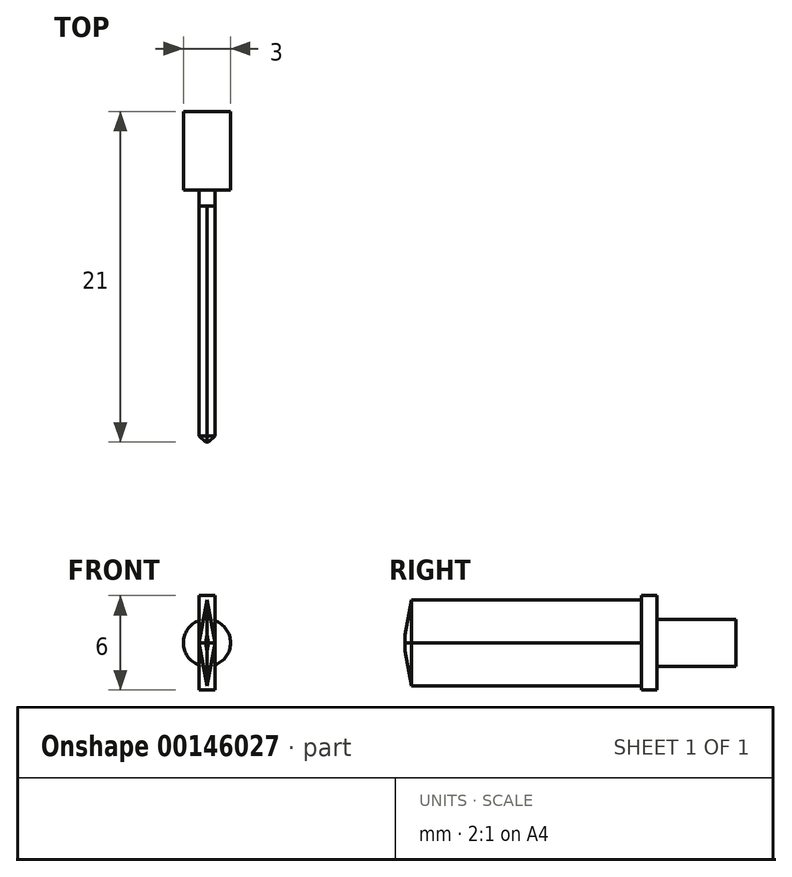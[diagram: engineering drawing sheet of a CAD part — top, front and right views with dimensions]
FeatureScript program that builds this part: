
annotation { "Feature Type Name" : "Feature", "Feature Type Description" : "" }
export const myFeature = defineFeature(function(context is Context, id is Id, definition is map)
    precondition{}
    {
        {
            var Q0;
            Q0=qCreatedBy(makeId("Front.planeOp"),FACE);
            var sketch = newSketch(context, id + "F0", { "sketchPlane" : qUnion([Q0])});
            skCircle(sketch, "E0", {"center": v(0, 0) * mm, "radius": 1.5 * mm});
            skSolve(sketch);
        }
        {
            var Q0;
            Q0 = qSketchRegion(id + "F0", true);
            extrude(context, id + "F1", {"entities" : qUnion([Q0]), "depth" : 5 * mm});
        }
        {
            var Q0;
            Q0=makeQuery(id+"F1.opExtrude","CAP_FACE",FACE,{"disambiguationData":[OSD([sQuery(id+"F0.wireOp",EDGE,"E0")])],"isStart":false});
            var sketch = newSketch(context, id + "F2", { "sketchPlane" : qUnion([Q0])});
            skLineSegment(sketch, "E1.bottom", {"start": v(0.5, 3) * mm, "end": v(-0.5, 3) * mm});
            skLineSegment(sketch, "E1.top", {"start": v(0.5, -3) * mm, "end": v(-0.5, -3) * mm});
            skLineSegment(sketch, "E1.left", {"start": v(0.5, 3) * mm, "end": v(0.5, -3) * mm});
            skLineSegment(sketch, "E1.right", {"start": v(-0.5, 3) * mm, "end": v(-0.5, -3) * mm});
            skPoint(sketch, "E1.middle", {"position": v(0, 0) * mm});
            skSolve(sketch);
        }
        {
            var Q0;
            Q0 = qSketchRegion(id + "F2", true);
            extrude(context, id + "F3", {"entities" : qUnion([Q0]), "operationType" : NewBodyOperationType.ADD, "depth" : 1 * mm});
        }
        {
            var Q0;
            Q0=makeQuery(id+"F3.opExtrude","CAP_FACE",FACE,{"disambiguationData":[OSD([sQuery(id+"F2.wireOp",EDGE,"E1.bottom"),sQuery(id+"F2.wireOp",EDGE,"E1.top"),sQuery(id+"F2.wireOp",EDGE,"E1.left"),sQuery(id+"F2.wireOp",EDGE,"E1.right")])],"isStart":false});
            var sketch = newSketch(context, id + "F4", { "sketchPlane" : qUnion([Q0])});
            skLineSegment(sketch, "E2", {"start": v(-0.5, 0) * mm, "end": v(0, 2.74) * mm});
            skLineSegment(sketch, "E3", {"start": v(0, 2.74) * mm, "end": v(0.5, 0) * mm});
            skLineSegment(sketch, "E4.MirrorCS", {"start": v(0, -2.74) * mm, "end": v(0.5, 0) * mm});
            skLineSegment(sketch, "E5.MirrorCS", {"start": v(-0.5, 0) * mm, "end": v(0, -2.74) * mm});
            skSolve(sketch);
        }
        {
            var Q0;
            Q0 = qSketchRegion(id + "F4", true);
            extrude(context, id + "F5", {"entities" : qUnion([Q0]), "operationType" : NewBodyOperationType.ADD, "depth" : 15 * mm});
        }
        {
            var Q0;
            Q0=makeQuery(id+"F5.opExtrude","CAP_EDGE",EDGE,{"disambiguationData":[OSD([sQuery(id+"F4.wireOp",EDGE,"E3")])],"isStart":false});
            var Q1;
            Q1=makeQuery(id+"F5.opExtrude","CAP_EDGE",EDGE,{"disambiguationData":[OSD([sQuery(id+"F4.wireOp",EDGE,"E4.MirrorCS")])],"isStart":false});
            var Q2;
            Q2=makeQuery(id+"F5.opExtrude","CAP_EDGE",EDGE,{"disambiguationData":[OSD([sQuery(id+"F4.wireOp",EDGE,"E2")])],"isStart":false});
            var Q3;
            Q3=makeQuery(id+"F5.opExtrude","CAP_EDGE",EDGE,{"disambiguationData":[OSD([sQuery(id+"F4.wireOp",EDGE,"E5.MirrorCS")])],"isStart":false});
            chamfer(context, id + "F6", {"entities" : qUnion([Q0, Q1, Q2, Q3]), "width" : 0.4 * mm, "tangentPropagation" : true});
        }
    });
